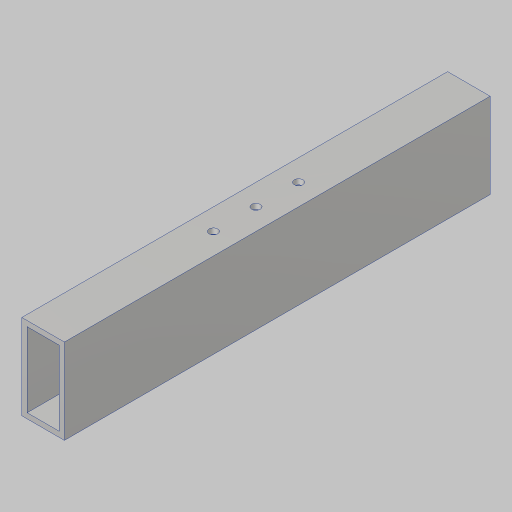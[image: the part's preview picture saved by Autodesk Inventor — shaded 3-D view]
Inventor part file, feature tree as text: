
AUTODESK INVENTOR PART (.ipt)
format: ipt  version: 2023.5 (Build 275446000, 446)  size: 109,568 bytes
history: native  units: in
note: dims shown in document units (in); Inventor stores cm internally (conversion verified against a paired STEP export)
features: extrude x1, hole x1, sketch x1
ambient origin geometry x8: Origin, YZ Plane, XZ Plane, XY Plane, X Axis, Y Axis, Z Axis, Center Point
bodies: Solid1 (feature_tree)
feature tree (3):
  extrude  "Extrusion1"  Depth=1.0in
  hole  "Hole1"  [1 undecoded]
  sketch  "Sketch2"  dims[d4=0.0in d5=1.0in d6=1.0in d7=0.201in d8=0.328in d9=0.385in d10=0.25in d11=0.5635in d12=1.0in d13=0.8108in]
note: 1 required parameter value undecoded (feature->parameter linkage not recoverable at this tier; creation-order binding heuristic only, values carry confidence <= 0.55)
